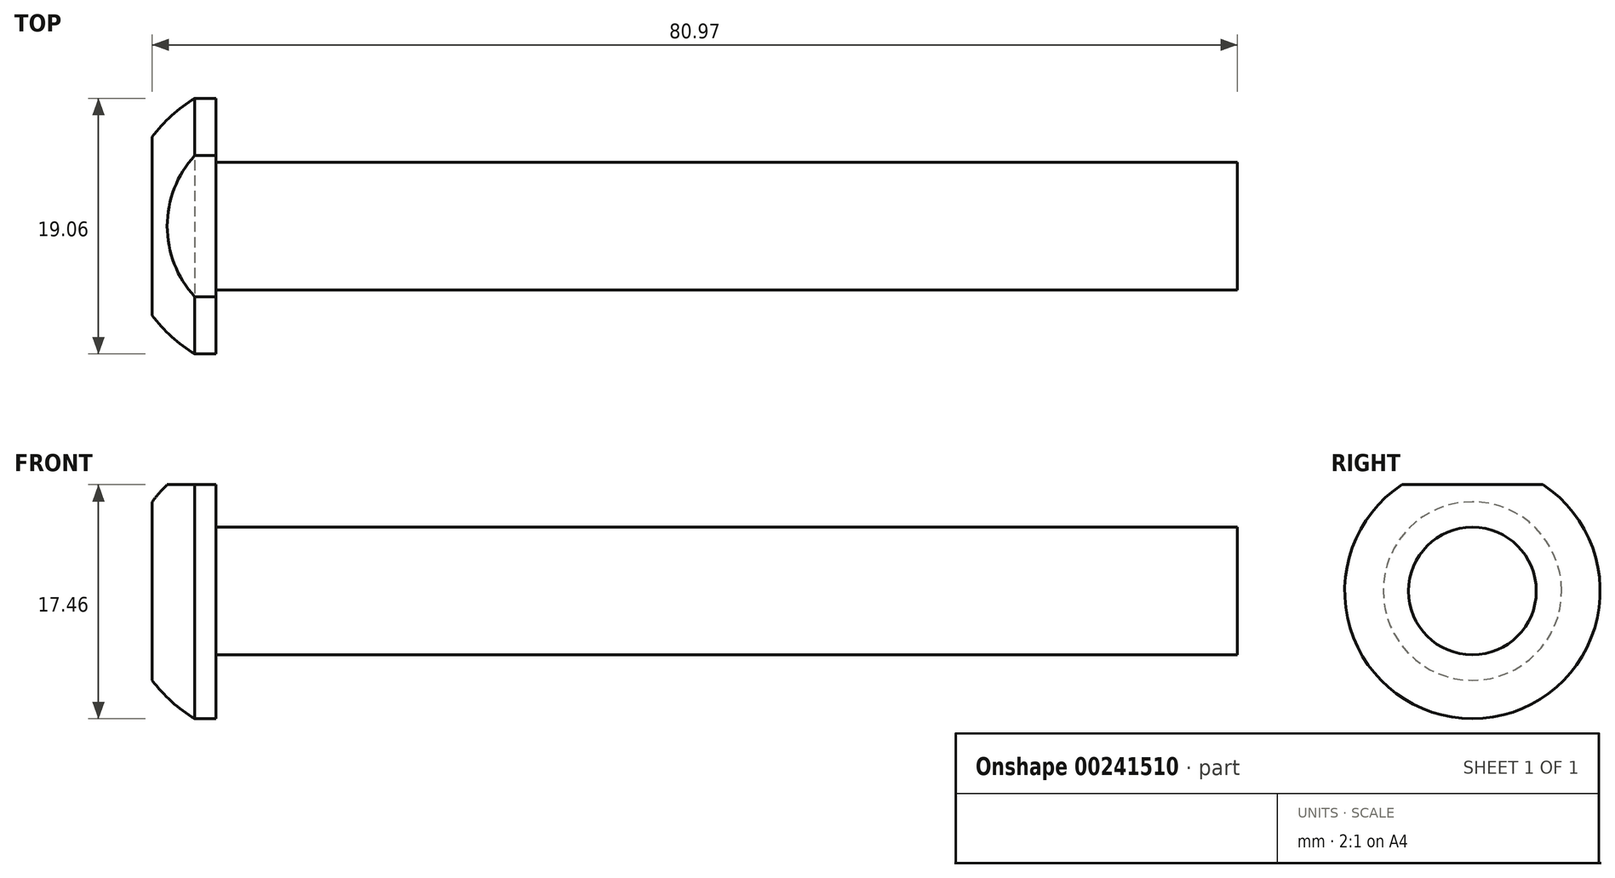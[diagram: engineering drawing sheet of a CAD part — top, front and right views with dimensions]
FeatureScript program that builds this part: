
annotation { "Feature Type Name" : "Feature", "Feature Type Description" : "" }
export const myFeature = defineFeature(function(context is Context, id is Id, definition is map)
    precondition{}
    {
        {
            var Q0;
            Q0=qCreatedBy(makeId("Front.planeOp"),FACE);
            var sketch = newSketch(context, id + "F0", { "sketchPlane" : qUnion([Q0])});
            skLineSegment(sketch, "E0.bottom", {"start": v(-6.02, 50.49) * mm, "end": v(-4.43, 50.49) * mm});
            skLineSegment(sketch, "E0.top", {"start": v(-6.02, 40.96) * mm, "end": v(-4.43, 40.96) * mm});
            skLineSegment(sketch, "E0.right", {"start": v(-4.43, 50.49) * mm, "end": v(-4.43, 45.73) * mm});
            skLineSegment(sketch, "E1.bottom", {"start": v(-4.43, 45.73) * mm, "end": v(71.77, 45.73) * mm});
            skLineSegment(sketch, "E1.top", {"start": v(-4.43, 40.96) * mm, "end": v(71.77, 40.96) * mm});
            skLineSegment(sketch, "E1.right", {"start": v(71.77, 45.73) * mm, "end": v(71.77, 40.96) * mm});
            skLineSegment(sketch, "E2.top", {"start": v(-6.02, 40.96) * mm, "end": v(-9.2, 40.96) * mm});
            skLineSegment(sketch, "E2.right", {"start": v(-9.2, 47.62) * mm, "end": v(-9.2, 40.96) * mm});
            skPoint(sketch, "E3", {"position": v(2.25, 40.96) * mm});
            skArc(sketch, "E4.trimOffspring", {"start": v(-6.02, 50.49) * mm, "mid": v(-7.75, 49.2) * mm, "end": v(-9.2, 47.62) * mm});
            skSolve(sketch);
        }
        {
            var Q0;
            Q0=makeQuery(id+"F0.imprint","IMPRINT",FACE,{"disambiguationData":[TD([[makeQuery(id+"F0.imprint","IMPRINT",EDGE,{"derivedFrom":sQuery(id+"F0.wireOp",EDGE,"E0.bottom")}),-1.0]])]});
            var Q1;
            Q1=sQuery(id+"F0.wireOp",EDGE,"E1.top");
            revolve(context, id + "F1", {"entities" : qUnion([Q0]), "axis" : qUnion([Q1]), "revolveType" : RevolveType.FULL});
        }
        {
            var Q0;
            Q0=makeQuery(id+"F1.opRevolve","SWEPT_FACE",FACE,{"disambiguationData":[OSD([sQuery(id+"F0.wireOp",EDGE,"E2.right")])]});
            var sketch = newSketch(context, id + "F2", { "sketchPlane" : qUnion([Q0])});
            skLineSegment(sketch, "E5", {"start": v(0, 40.96) * mm, "end": v(0, 48.9) * mm});
            skLineSegment(sketch, "E6", {"start": v(0, 48.9) * mm, "end": v(19.3, 48.9) * mm});
            skLineSegment(sketch, "E7.bottom", {"start": v(19.3, 48.9) * mm, "end": v(-27.42, 48.9) * mm});
            skLineSegment(sketch, "E7.top", {"start": v(19.3, 53.73) * mm, "end": v(-27.42, 53.73) * mm});
            skLineSegment(sketch, "E7.left", {"start": v(19.3, 48.9) * mm, "end": v(19.3, 53.73) * mm});
            skLineSegment(sketch, "E7.right", {"start": v(-27.42, 48.9) * mm, "end": v(-27.42, 53.73) * mm});
            skSolve(sketch);
        }
        {
            var Q0;
            Q0 = qSketchRegion(id + "F2", true);
            extrude(context, id + "F3", {"entities" : qUnion([Q0]), "operationType" : NewBodyOperationType.REMOVE, "oppositeDirection" : true, "depth" : 25.4 * mm});
        }
    });
